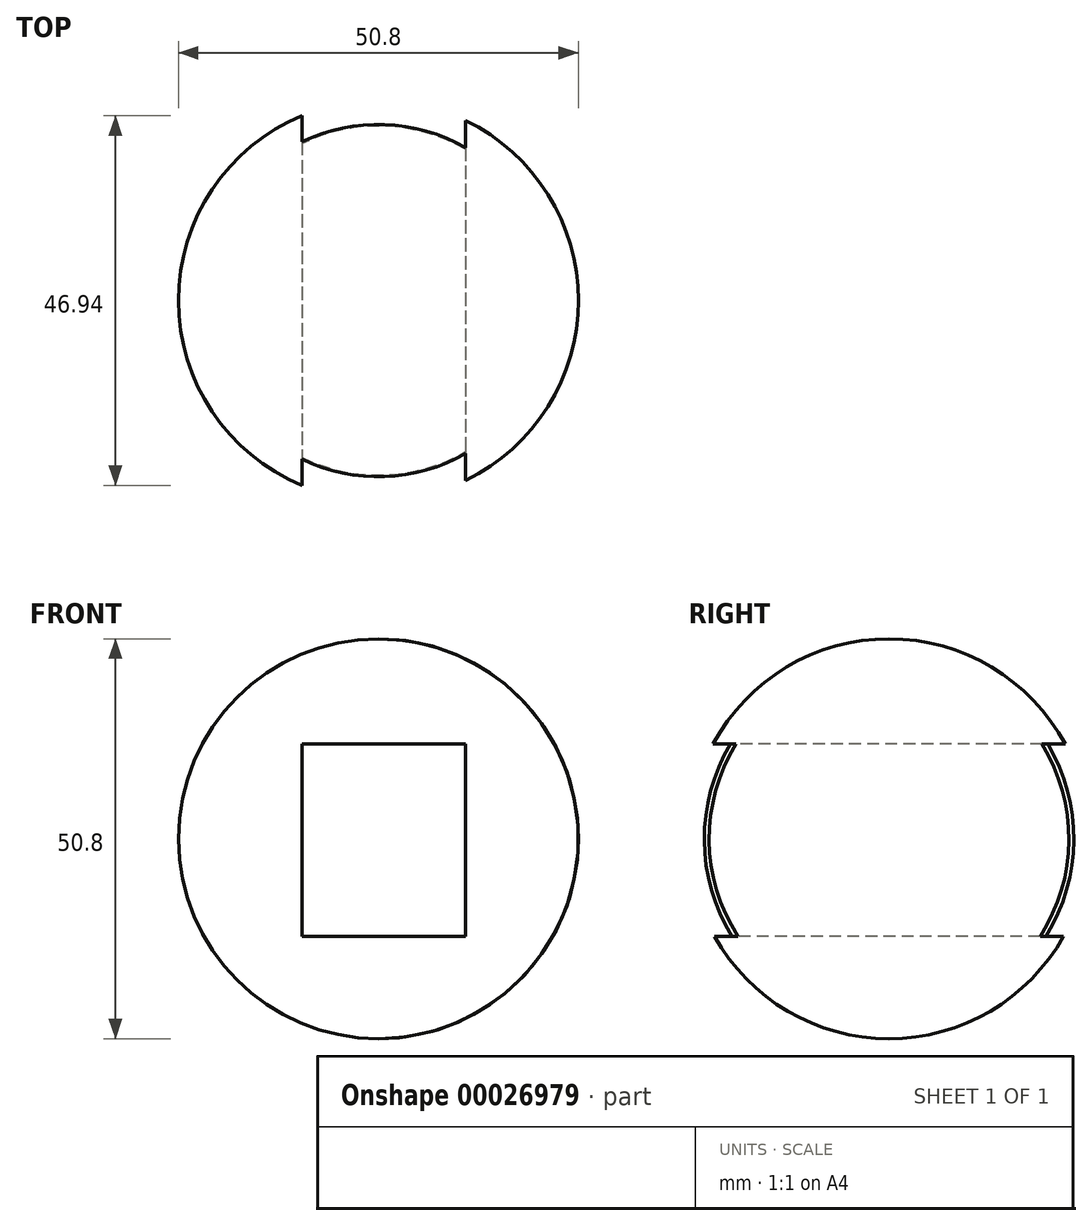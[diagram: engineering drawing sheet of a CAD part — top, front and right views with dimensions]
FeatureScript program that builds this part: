
annotation { "Feature Type Name" : "Feature", "Feature Type Description" : "" }
export const myFeature = defineFeature(function(context is Context, id is Id, definition is map)
    precondition{}
    {
        {
            var Q0;
            Q0=qCreatedBy(makeId("Front.planeOp"),FACE);
            var sketch = newSketch(context, id + "F0", { "sketchPlane" : qUnion([Q0])});
            skLineSegment(sketch, "E0", {"start": v(-0.57, 25.7) * mm, "end": v(-0.57, -25.1) * mm});
            skArc(sketch, "E1", {"start": v(-0.57, -25.1) * mm, "mid": v(24.83, 0.3) * mm, "end": v(-0.57, 25.7) * mm});
            skSolve(sketch);
        }
        {
            var Q0;
            Q0=makeQuery(id+"F0.imprint","IMPRINT",FACE,{"disambiguationData":[TD([[makeQuery(id+"F0.imprint","IMPRINT",EDGE,{"derivedFrom":sQuery(id+"F0.wireOp",EDGE,"E0")}),1.0]])]});
            var Q1;
            Q1=sQuery(id+"F0.wireOp",EDGE,"E0");
            revolve(context, id + "F1", {"entities" : qUnion([Q0]), "axis" : qUnion([Q1]), "revolveType" : RevolveType.FULL});
        }
        {
            var Q0;
            Q0=qCreatedBy(makeId("Front.planeOp"),FACE);
            cPlane(context, id + "F2", {"entities" : qUnion([Q0]), "cplaneType" : CPlaneType.OFFSET, "offset" : 25.4 * mm, "width" : 152.4 * mm, "height" : 152.4 * mm});
        }
        {
            var Q0;
            Q0=qCreatedBy(id+"F2.planeOp",FACE);
            var sketch = newSketch(context, id + "F3", { "sketchPlane" : qUnion([Q0])});
            skLineSegment(sketch, "E2.bottom", {"start": v(-76.3, 75.94) * mm, "end": v(76.3, 75.94) * mm});
            skLineSegment(sketch, "E2.top", {"start": v(-76.3, -76.66) * mm, "end": v(76.3, -76.66) * mm});
            skLineSegment(sketch, "E2.left", {"start": v(-76.3, 75.94) * mm, "end": v(-76.3, -76.66) * mm});
            skLineSegment(sketch, "E2.right", {"start": v(76.3, 75.94) * mm, "end": v(76.3, -76.66) * mm});
            skPoint(sketch, "E3.start.orphan", {"position": v(0, 75.94) * mm});
            skPoint(sketch, "E4.start.orphan", {"position": v(-76.3, -0.36) * mm});
            skPoint(sketch, "E5.trimOffspring.end.orphan", {"position": v(76.3, -0.36) * mm});
            skPoint(sketch, "E6.trimOffspring.end.orphan", {"position": v(0, -76.66) * mm});
            skLineSegment(sketch, "E7.bottom", {"start": v(-10.29, 12.32) * mm, "end": v(10.52, 12.32) * mm});
            skLineSegment(sketch, "E7.top", {"start": v(-10.29, -12.08) * mm, "end": v(10.52, -12.08) * mm});
            skLineSegment(sketch, "E7.left", {"start": v(-10.29, 12.32) * mm, "end": v(-10.29, -12.08) * mm});
            skLineSegment(sketch, "E7.right", {"start": v(10.52, 12.32) * mm, "end": v(10.52, -12.08) * mm});
            skSolve(sketch);
        }
        {
            var Q0;
            Q0=makeQuery(id+"F3.imprint","IMPRINT",FACE,{"disambiguationData":[TD([[makeQuery(id+"F3.imprint","IMPRINT",EDGE,{"derivedFrom":sQuery(id+"F3.wireOp",EDGE,"E7.bottom")}),-1.0]])]});
            extrude(context, id + "F4", {"entities" : qUnion([Q0]), "operationType" : NewBodyOperationType.REMOVE, "oppositeDirection" : true, "depth" : 50.8 * mm});
        }
    });
